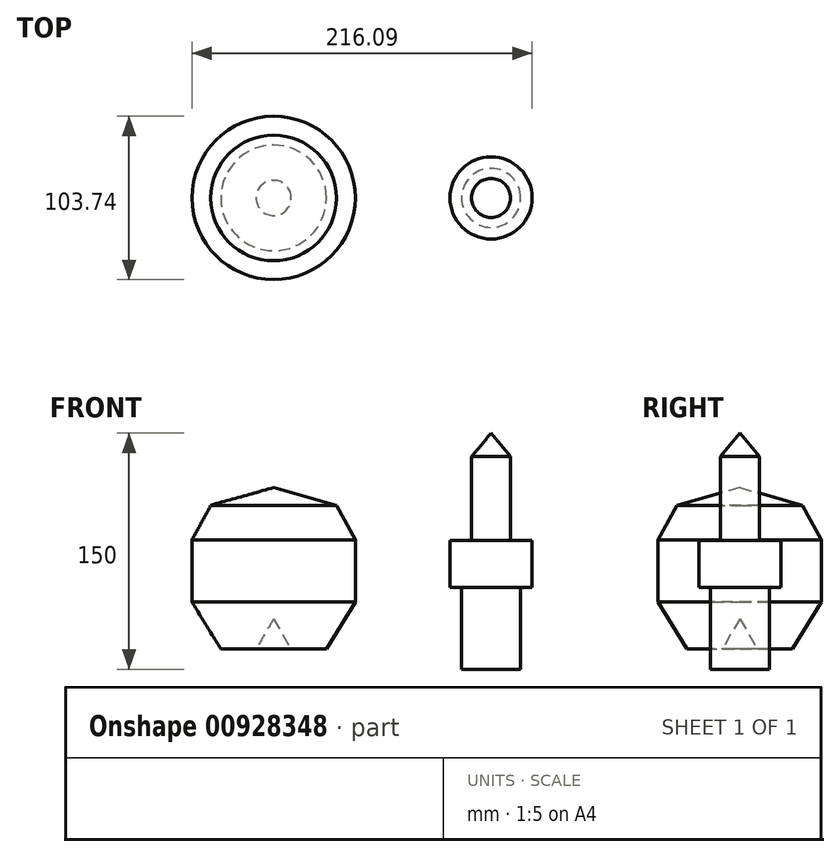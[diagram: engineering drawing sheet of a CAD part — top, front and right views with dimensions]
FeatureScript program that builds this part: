
annotation { "Feature Type Name" : "Feature", "Feature Type Description" : "" }
export const myFeature = defineFeature(function(context is Context, id is Id, definition is map)
    precondition{}
    {
        {
            var Q0;
            Q0=qCreatedBy(makeId("Front.planeOp"),FACE);
            var sketch = newSketch(context, id + "F0", { "sketchPlane" : qUnion([Q0])});
            skLineSegment(sketch, "E0", {"start": v(0, 56.1) * mm, "end": v(39.9, 44.92) * mm});
            skLineSegment(sketch, "E1", {"start": v(39.9, 44.92) * mm, "end": v(51.87, 22.98) * mm});
            skLineSegment(sketch, "E2", {"start": v(51.87, 22.98) * mm, "end": v(51.87, -16.51) * mm});
            skLineSegment(sketch, "E3", {"start": v(51.87, -16.51) * mm, "end": v(33.52, -46.43) * mm});
            skLineSegment(sketch, "E4", {"start": v(33.52, -46.43) * mm, "end": v(11.18, -46.43) * mm});
            skLineSegment(sketch, "E5", {"start": v(11.18, -46.43) * mm, "end": v(0, -27.29) * mm});
            skLineSegment(sketch, "E6", {"start": v(0, -27.29) * mm, "end": v(0, 56.1) * mm});
            skLineSegment(sketch, "E7", {"start": v(138.12, 90.73) * mm, "end": v(150.49, 75.73) * mm});
            skLineSegment(sketch, "E8", {"start": v(150.49, 75.73) * mm, "end": v(150.49, 22.61) * mm});
            skLineSegment(sketch, "E9", {"start": v(150.49, 22.61) * mm, "end": v(164.22, 22.61) * mm});
            skLineSegment(sketch, "E10", {"start": v(164.22, 22.61) * mm, "end": v(164.22, -7.39) * mm});
            skLineSegment(sketch, "E11", {"start": v(164.22, -7.39) * mm, "end": v(156.87, -7.39) * mm});
            skLineSegment(sketch, "E12", {"start": v(156.87, -7.39) * mm, "end": v(156.87, -59.27) * mm});
            skLineSegment(sketch, "E13", {"start": v(156.87, -59.27) * mm, "end": v(138.12, -59.27) * mm});
            skLineSegment(sketch, "E14", {"start": v(138.12, -59.27) * mm, "end": v(138.12, 90.73) * mm});
            skSolve(sketch);
        }
        {
            var Q0;
            Q0=makeQuery(id+"F0.imprint","IMPRINT",FACE,{"disambiguationData":[TD([[makeQuery(id+"F0.imprint","IMPRINT",EDGE,{"derivedFrom":sQuery(id+"F0.wireOp",EDGE,"E0")}),-1.0]])]});
            var Q1;
            Q1=sQuery(id+"F0.wireOp",EDGE,"E6");
            revolve(context, id + "F1", {"surfaceOperationType" : NewSurfaceOperationType.NEW, "entities" : qUnion([Q0]), "axis" : qUnion([Q1]), "revolveType" : RevolveType.FULL});
        }
        {
            var Q0;
            Q0=makeQuery(id+"F0.imprint","IMPRINT",FACE,{"disambiguationData":[TD([[makeQuery(id+"F0.imprint","IMPRINT",EDGE,{"derivedFrom":sQuery(id+"F0.wireOp",EDGE,"E7")}),-1.0]])]});
            var Q1;
            Q1=sQuery(id+"F0.wireOp",EDGE,"E14");
            revolve(context, id + "F2", {"surfaceOperationType" : NewSurfaceOperationType.NEW, "entities" : qUnion([Q0]), "axis" : qUnion([Q1]), "revolveType" : RevolveType.FULL});
        }
    });
